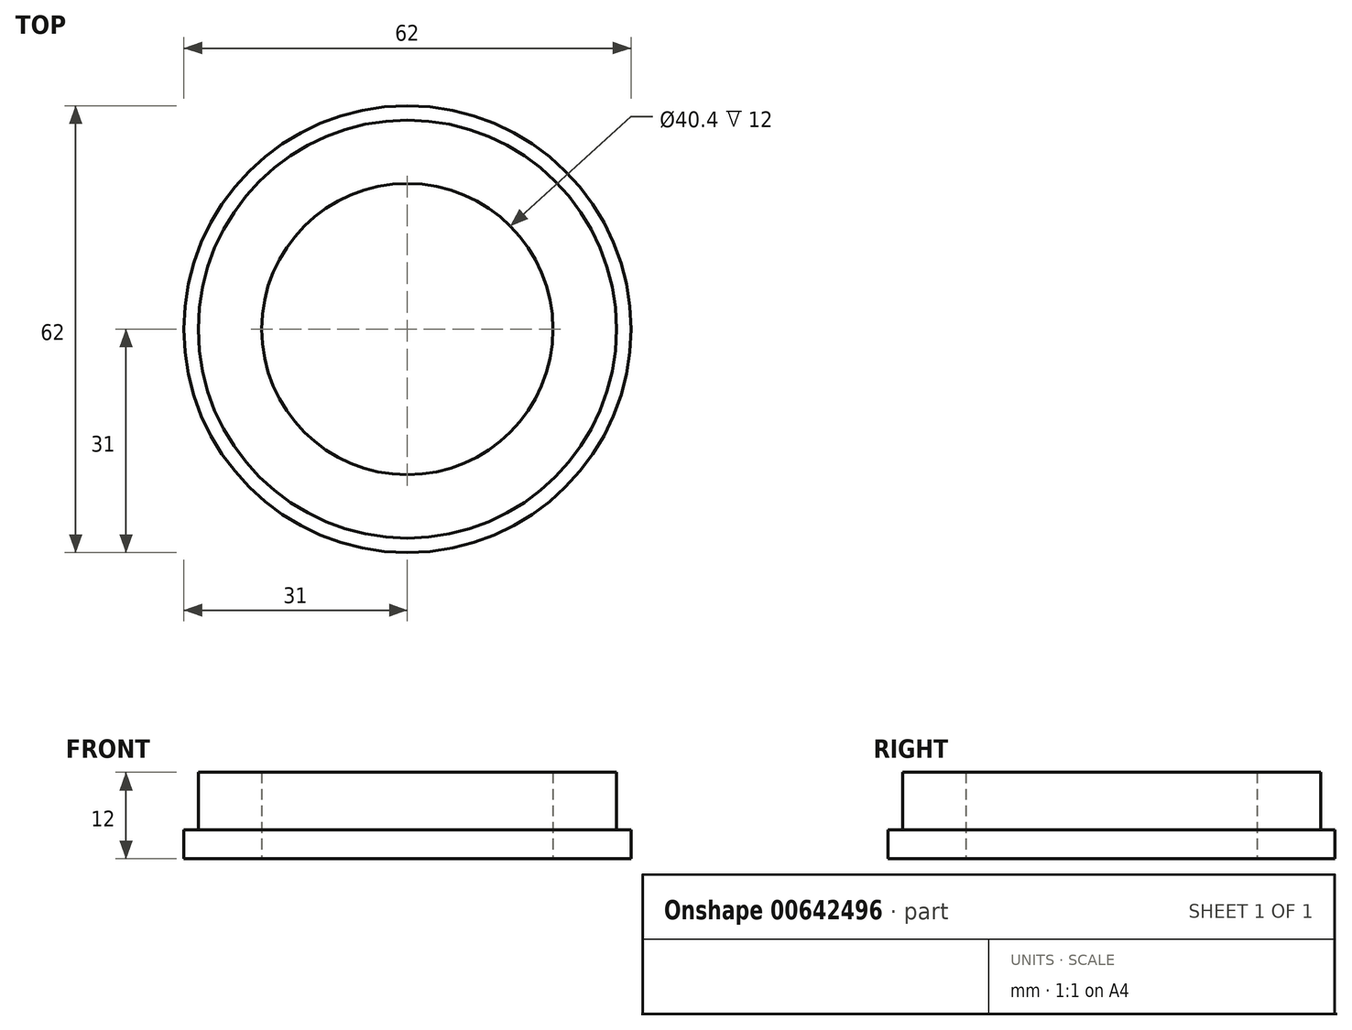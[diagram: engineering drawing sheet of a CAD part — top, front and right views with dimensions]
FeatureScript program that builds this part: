
annotation { "Feature Type Name" : "Feature", "Feature Type Description" : "" }
export const myFeature = defineFeature(function(context is Context, id is Id, definition is map)
    precondition{}
    {
        {
            var Q0;
            Q0=qCreatedBy(makeId("Top.planeOp"),FACE);
            var sketch = newSketch(context, id + "F0", { "sketchPlane" : qUnion([Q0])});
            skCircle(sketch, "E0", {"center": v(0, 0) * mm, "radius": 20.2 * mm});
            skCircle(sketch, "E1", {"center": v(0, 0) * mm, "radius": 29 * mm});
            skCircle(sketch, "E2", {"center": v(0, 0) * mm, "radius": 31 * mm});
            skSolve(sketch);
        }
        {
            var Q0;
            Q0=makeQuery(id+"F0.imprint","IMPRINT",FACE,{"disambiguationData":[TD([[makeQuery(id+"F0.imprint","IMPRINT",EDGE,{"derivedFrom":sQuery(id+"F0.wireOp",EDGE,"E0")}),-1.0]])]});
            extrude(context, id + "F1", {"entities" : qUnion([Q0]), "depth" : 8 * mm, "offsetDistance" : 25 * mm});
        }
        {
            var Q0;
            Q0=makeQuery(id+"F0.imprint","IMPRINT",FACE,{"disambiguationData":[TD([[makeQuery(id+"F0.imprint","IMPRINT",EDGE,{"derivedFrom":sQuery(id+"F0.wireOp",EDGE,"E1")}),-1.0]])]});
            var Q1;
            Q1=makeQuery(id+"F1.opExtrude","CAP_FACE",FACE,{"disambiguationData":[OSD([sQuery(id+"F0.wireOp",EDGE,"E0"),sQuery(id+"F0.wireOp",EDGE,"E1")])],"isStart":true});
            extrude(context, id + "F2", {"entities" : qUnion([Q0, Q1]), "operationType" : NewBodyOperationType.ADD, "oppositeDirection" : true, "depth" : 4 * mm, "offsetDistance" : 25 * mm});
        }
    });
